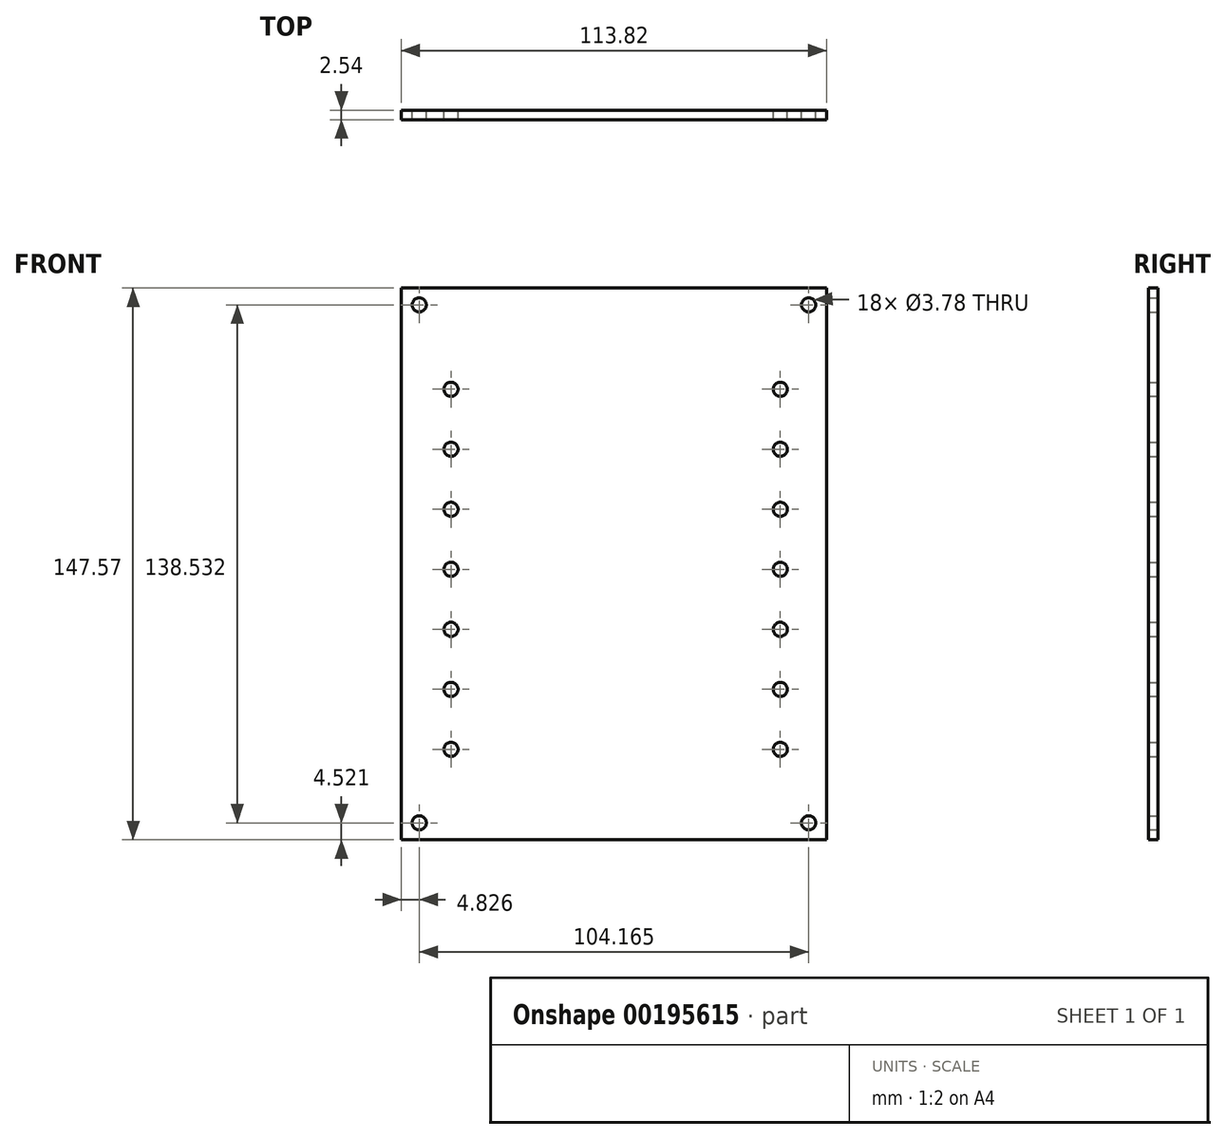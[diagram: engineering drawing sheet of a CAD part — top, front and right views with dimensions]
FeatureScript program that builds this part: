
annotation { "Feature Type Name" : "Feature", "Feature Type Description" : "" }
export const myFeature = defineFeature(function(context is Context, id is Id, definition is map)
    precondition{}
    {
        {
            var Q0;
            Q0=qCreatedBy(makeId("Front.planeOp"),FACE);
            var sketch = newSketch(context, id + "F0", { "sketchPlane" : qUnion([Q0])});
            skLineSegment(sketch, "E0.bottom", {"start": v(0, 0) * mm, "end": v(113.82, 0) * mm});
            skLineSegment(sketch, "E0.top", {"start": v(0, 147.57) * mm, "end": v(113.82, 147.57) * mm});
            skLineSegment(sketch, "E0.left", {"start": v(0, 0) * mm, "end": v(0, 147.57) * mm});
            skLineSegment(sketch, "E0.right", {"start": v(113.82, 0) * mm, "end": v(113.82, 147.57) * mm});
            skCircle(sketch, "E1", {"center": v(4.83, 4.52) * mm, "radius": 1.9 * mm});
            skLineSegment(sketch, "E2", {"start": v(4.83, 4.52) * mm, "end": v(0, 4.52) * mm});
            skLineSegment(sketch, "E3", {"start": v(4.83, 4.52) * mm, "end": v(4.83, 0) * mm});
            skLineSegment(sketch, "E4.bottom", {"start": v(113.82, 0) * mm, "end": v(109, 0) * mm});
            skLineSegment(sketch, "E4.top", {"start": v(113.82, 4.52) * mm, "end": v(109, 4.52) * mm});
            skLineSegment(sketch, "E4.left", {"start": v(113.82, 0) * mm, "end": v(113.82, 4.52) * mm});
            skLineSegment(sketch, "E4.right", {"start": v(109, 0) * mm, "end": v(109, 4.52) * mm});
            skCircle(sketch, "E5", {"center": v(109, 4.52) * mm, "radius": 1.9 * mm});
            skLineSegment(sketch, "E6.bottom", {"start": v(0, 147.57) * mm, "end": v(4.83, 147.57) * mm});
            skLineSegment(sketch, "E6.top", {"start": v(0, 143.05) * mm, "end": v(4.83, 143.05) * mm});
            skLineSegment(sketch, "E6.left", {"start": v(0, 147.57) * mm, "end": v(0, 143.05) * mm});
            skLineSegment(sketch, "E6.right", {"start": v(4.83, 147.57) * mm, "end": v(4.83, 143.05) * mm});
            skCircle(sketch, "E7", {"center": v(4.83, 143.05) * mm, "radius": 1.9 * mm});
            skLineSegment(sketch, "E8.bottom", {"start": v(113.82, 147.57) * mm, "end": v(109, 147.57) * mm});
            skLineSegment(sketch, "E8.top", {"start": v(113.82, 143.05) * mm, "end": v(109, 143.05) * mm});
            skLineSegment(sketch, "E8.left", {"start": v(113.82, 147.57) * mm, "end": v(113.82, 143.05) * mm});
            skLineSegment(sketch, "E8.right", {"start": v(109, 147.57) * mm, "end": v(109, 143.05) * mm});
            skCircle(sketch, "E9", {"center": v(109, 143.05) * mm, "radius": 1.9 * mm});
            skCircle(sketch, "E10", {"center": v(13.32, 120.48) * mm, "radius": 1.9 * mm});
            skCircle(sketch, "E11.0.1.0", {"center": v(13.32, 104.43) * mm, "radius": 1.9 * mm});
            skCircle(sketch, "E11.0.2.0", {"center": v(13.32, 88.38) * mm, "radius": 1.9 * mm});
            skCircle(sketch, "E11.0.3.0", {"center": v(13.32, 72.33) * mm, "radius": 1.9 * mm});
            skCircle(sketch, "E11.0.4.0", {"center": v(13.32, 56.27) * mm, "radius": 1.9 * mm});
            skCircle(sketch, "E11.0.5.0", {"center": v(13.32, 40.22) * mm, "radius": 1.9 * mm});
            skCircle(sketch, "E11.0.6.0", {"center": v(13.32, 24.17) * mm, "radius": 1.9 * mm});
            skLineSegment(sketch, "E11.direction1", {"start": v(13.67, 123.24) * mm, "end": v(25.25, 123.24) * mm, "construction": true});
            skLineSegment(sketch, "E11.direction2", {"start": v(13.67, 123.24) * mm, "end": v(13.67, 111.66) * mm, "construction": true});
            skLineSegment(sketch, "E12", {"start": v(13.32, 24.17) * mm, "end": v(15.21, 24.17) * mm});
            skCircle(sketch, "E13", {"center": v(101.4, 24.17) * mm, "radius": 1.9 * mm});
            skCircle(sketch, "E14.0.1.0", {"center": v(101.4, 40.22) * mm, "radius": 1.9 * mm});
            skCircle(sketch, "E14.0.2.0", {"center": v(101.4, 56.27) * mm, "radius": 1.9 * mm});
            skCircle(sketch, "E14.0.3.0", {"center": v(101.4, 72.33) * mm, "radius": 1.9 * mm});
            skCircle(sketch, "E14.0.4.0", {"center": v(101.4, 88.38) * mm, "radius": 1.9 * mm});
            skCircle(sketch, "E14.0.5.0", {"center": v(101.4, 104.43) * mm, "radius": 1.9 * mm});
            skCircle(sketch, "E14.0.6.0", {"center": v(101.4, 120.48) * mm, "radius": 1.9 * mm});
            skLineSegment(sketch, "E14.direction1", {"start": v(101.4, 24.17) * mm, "end": v(103.3, 24.17) * mm, "construction": true});
            skLineSegment(sketch, "E14.direction2", {"start": v(101.4, 24.17) * mm, "end": v(101.4, 40.22) * mm, "construction": true});
            skLineSegment(sketch, "E15.trimOffspring", {"start": v(99.52, 24.17) * mm, "end": v(101.4, 24.17) * mm});
            skLineSegment(sketch, "E16", {"start": v(13.32, 24.17) * mm, "end": v(101.4, 24.17) * mm});
            skSolve(sketch);
        }
        {
            var Q0;
            Q0 = qSketchRegion(id + "F0", true);
            extrude(context, id + "F1", {"entities" : qUnion([Q0]), "depth" : 2.54 * mm});
        }
    });
